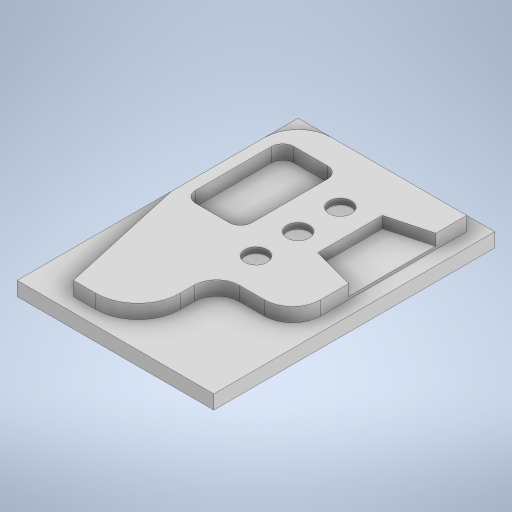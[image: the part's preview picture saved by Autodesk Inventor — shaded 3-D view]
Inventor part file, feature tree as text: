
AUTODESK INVENTOR PART (.ipt)
format: ipt  version: 2023.2 (Build 272271000, 271)  size: 308,736 bytes
history: native  units: mm
features: extrude x4, sketch x4
ambient origin geometry x8: Origin, YZ Plane, XZ Plane, XY Plane, X Axis, Y Axis, Z Axis, Center Point
bodies: Solid1 (feature_tree)
feature tree (8):
  extrude  "Extrusion1"  Depth=100.0mm
  extrude  "Extrusion2"  Depth=60.0mm
  extrude  "Extrusion3"  Depth=50.0mm
  extrude  "Extrusion4"  Depth=32.0mm
  sketch  "Sketch1"  dims[d0=70.0mm d1=100.0mm]
  sketch  "Sketch2"  dims[d2=5.0mm d3=0.0mm d4=60.0mm]
  sketch  "Sketch3"  dims[d5=90.0mm d6=50.0mm]
  sketch  "Sketch4"  dims[d7=55.0mm d8=32.0mm d9=33.0mm d10=8.0mm d11=10.0mm d12=12.0mm d13=5.0mm d14=0.0mm d15=23.0mm d16=15.0mm d17=53.0mm d18=57.0mm d19=84.0mm d20=4.0mm d21=0.0mm d22=20.0mm d23=35.0mm d24=68.0mm d25=51.0mm d26=15.0mm d27=8.0mm d28=45.0mm d29=30.0mm d30=30.0mm d32=15.0mm d33=10.0mm d35=10.0mm d37=2.0mm d38=0.0mm d39=4.0mm]
